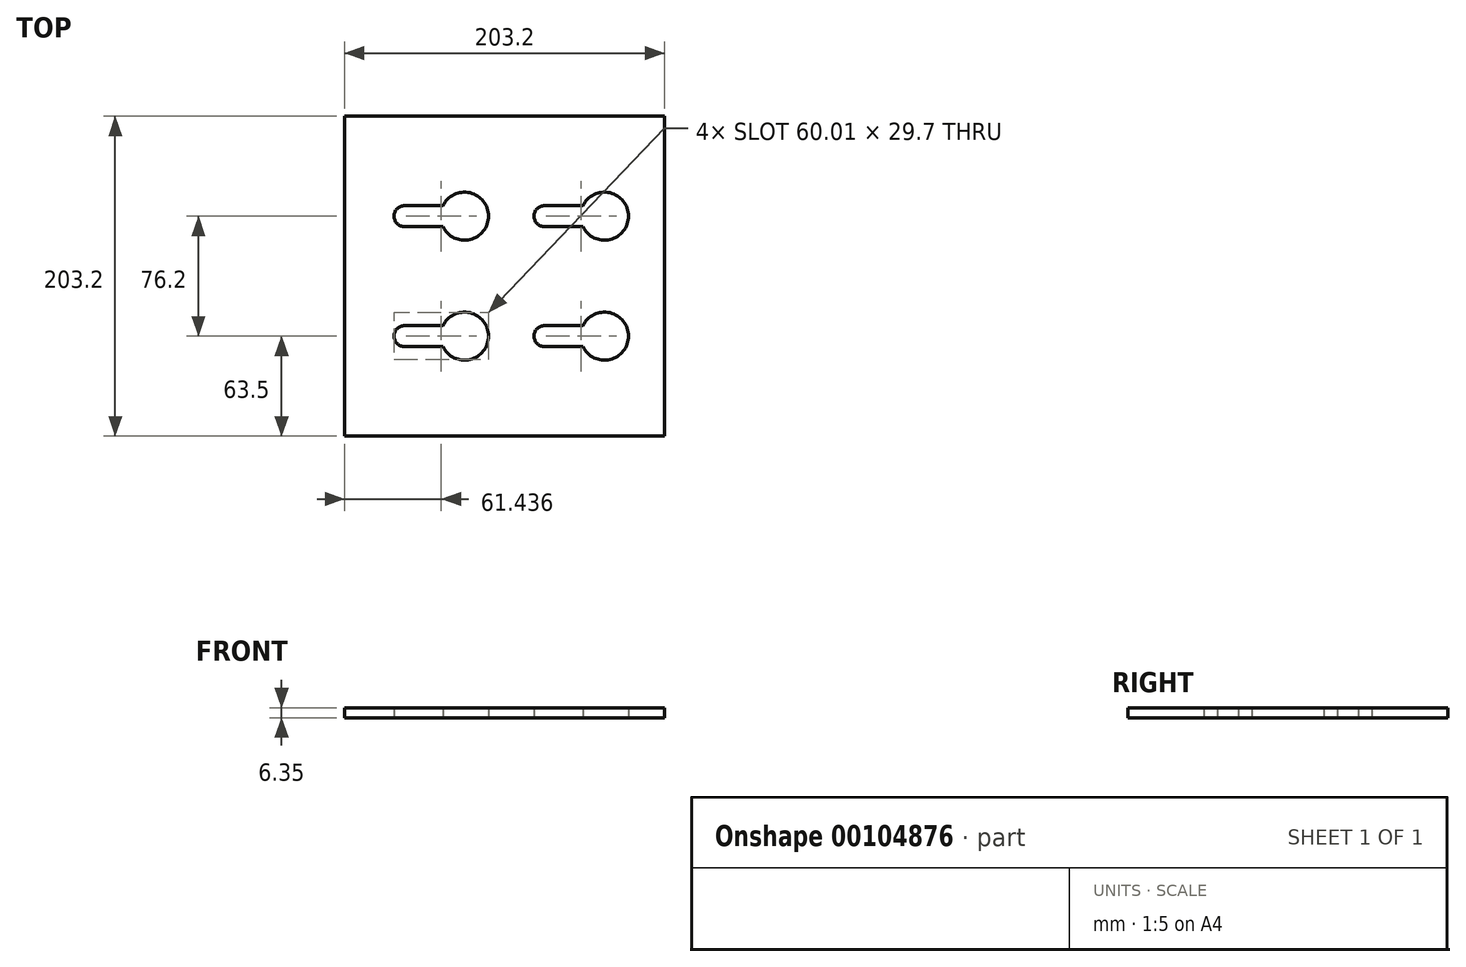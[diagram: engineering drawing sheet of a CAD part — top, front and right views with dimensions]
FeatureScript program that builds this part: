
annotation { "Feature Type Name" : "Feature", "Feature Type Description" : "" }
export const myFeature = defineFeature(function(context is Context, id is Id, definition is map)
    precondition{}
    {
        {
            var Q0;
            Q0=qCreatedBy(makeId("Top.planeOp"),FACE);
            var sketch = newSketch(context, id + "F0", { "sketchPlane" : qUnion([Q0])});
            skCircle(sketch, "E0", {"center": v(63.5, 38.1) * mm, "radius": 15.24 * mm});
            skCircle(sketch, "E1", {"center": v(-25.4, 38.1) * mm, "radius": 15.24 * mm});
            skCircle(sketch, "E2", {"center": v(-63.5, 38.1) * mm, "radius": 6.67 * mm});
            skCircle(sketch, "E3", {"center": v(25.4, 38.1) * mm, "radius": 6.67 * mm});
            skLineSegment(sketch, "E4.bottom", {"start": v(-101.6, 101.6) * mm, "end": v(101.6, 101.6) * mm});
            skLineSegment(sketch, "E4.top", {"start": v(-101.6, -101.6) * mm, "end": v(101.6, -101.6) * mm});
            skLineSegment(sketch, "E4.left", {"start": v(-101.6, 101.6) * mm, "end": v(-101.6, -101.6) * mm});
            skLineSegment(sketch, "E4.right", {"start": v(101.6, 101.6) * mm, "end": v(101.6, -101.6) * mm});
            skPoint(sketch, "E4.middle", {"position": v(0, 0) * mm});
            skLineSegment(sketch, "E5", {"start": v(-63.5, 44.77) * mm, "end": v(-39.1, 44.77) * mm});
            skLineSegment(sketch, "E6", {"start": v(-63.5, 31.43) * mm, "end": v(-39.1, 31.43) * mm});
            skLineSegment(sketch, "E7", {"start": v(25.4, 44.77) * mm, "end": v(49.8, 44.77) * mm});
            skLineSegment(sketch, "E8", {"start": v(25.4, 31.43) * mm, "end": v(49.8, 31.43) * mm});
            skCircle(sketch, "E9.MirrorC", {"center": v(25.4, -38.1) * mm, "radius": 6.67 * mm});
            skLineSegment(sketch, "E10.MirrorCS", {"start": v(-63.5, -44.77) * mm, "end": v(-39.1, -44.77) * mm});
            skLineSegment(sketch, "E11.MirrorCS", {"start": v(-63.5, -31.43) * mm, "end": v(-39.1, -31.43) * mm});
            skLineSegment(sketch, "E12.MirrorCS", {"start": v(25.4, -31.43) * mm, "end": v(49.8, -31.43) * mm});
            skLineSegment(sketch, "E13.MirrorCS", {"start": v(25.4, -44.77) * mm, "end": v(49.8, -44.77) * mm});
            skCircle(sketch, "E14.MirrorC", {"center": v(-63.5, -38.1) * mm, "radius": 6.67 * mm});
            skCircle(sketch, "E15.MirrorC", {"center": v(-25.4, -38.1) * mm, "radius": 15.24 * mm});
            skCircle(sketch, "E16.MirrorC", {"center": v(63.5, -38.1) * mm, "radius": 15.24 * mm});
            skSolve(sketch);
        }
        {
            var Q0;
            Q0=makeQuery(id+"F0.imprint","IMPRINT",FACE,{"disambiguationData":[TD([[makeQuery(id+"F0.imprint","IMPRINT",EDGE,{"derivedFrom":sQuery(id+"F0.wireOp",EDGE,"E4.bottom")}),-1.0]])]});
            extrude(context, id + "F1", {"entities" : qUnion([Q0]), "depth" : 6.35 * mm});
        }
    });
